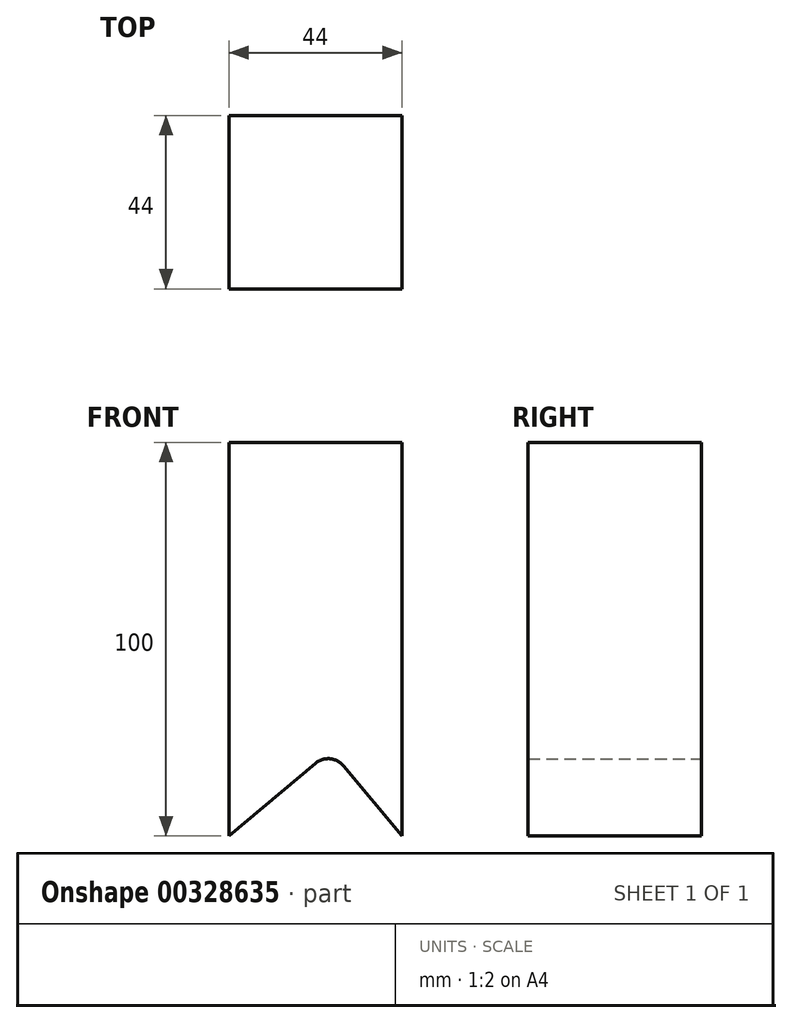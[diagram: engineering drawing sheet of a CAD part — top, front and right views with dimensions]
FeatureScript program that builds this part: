
annotation { "Feature Type Name" : "Feature", "Feature Type Description" : "" }
export const myFeature = defineFeature(function(context is Context, id is Id, definition is map)
    precondition{}
    {
        {
            var Q0;
            Q0=qCreatedBy(makeId("Top.planeOp"),FACE);
            var sketch = newSketch(context, id + "F0", { "sketchPlane" : qUnion([Q0])});
            skLineSegment(sketch, "E0.bottom", {"start": v(22, -22) * mm, "end": v(-22, -22) * mm});
            skLineSegment(sketch, "E0.top", {"start": v(22, 22) * mm, "end": v(-22, 22) * mm});
            skLineSegment(sketch, "E0.left", {"start": v(22, -22) * mm, "end": v(22, 22) * mm});
            skLineSegment(sketch, "E0.right", {"start": v(-22, -22) * mm, "end": v(-22, 22) * mm});
            skPoint(sketch, "E0.middle", {"position": v(0, 0) * mm});
            skSolve(sketch);
        }
        {
            var Q0;
            Q0=qSketchRegion(id+"F0",true);
            extrude(context, id + "F1", {"entities" : qUnion([Q0]), "depth" : 100 * mm});
        }
        {
            var Q0;
            Q0=makeQuery(id+"F1.opExtrude","SWEPT_FACE",FACE,{"disambiguationData":[OSD([sQuery(id+"F0.wireOp",EDGE,"E0.bottom")])]});
            var sketch = newSketch(context, id + "F2", { "sketchPlane" : qUnion([Q0])});
            skLineSegment(sketch, "E1", {"start": v(-22, 0) * mm, "end": v(3.82, 21.67) * mm});
            skLineSegment(sketch, "E2", {"start": v(3.82, 21.67) * mm, "end": v(22, 0) * mm});
            skSolve(sketch);
        }
        {
            var Q0;
            Q0=makeQuery(id+"F2.imprint","IMPRINT",FACE,{"disambiguationData":[TD([[makeQuery(id+"F2.imprint","IMPRINT",EDGE,{"derivedFrom":sQuery(id+"F2.wireOp",EDGE,"E1")}),-1.0]])]});
            extrude(context, id + "F3", {"entities" : qUnion([Q0]), "operationType" : NewBodyOperationType.REMOVE, "endBound" : BoundingType.THROUGH_ALL, "oppositeDirection" : true, "depth" : 25 * mm});
        }
        {
            var Q0;
            Q0=makeQuery(id+"F3.boolean.opBoolean","COPY",EDGE,{"derivedFrom":makeQuery(id+"F3.opExtrude","SWEPT_EDGE",EDGE,{"disambiguationData":[OSD([sQuery(id+"F2.wireOp",EDGE,"E1"),sQuery(id+"F2.wireOp",EDGE,"E2")])]})});
            fillet(context, id + "F4", {"entities" : qUnion([Q0]), "radius" : 5 * mm, "tangentPropagation" : true, "allowEdgeOverflow" : false});
        }
    });
